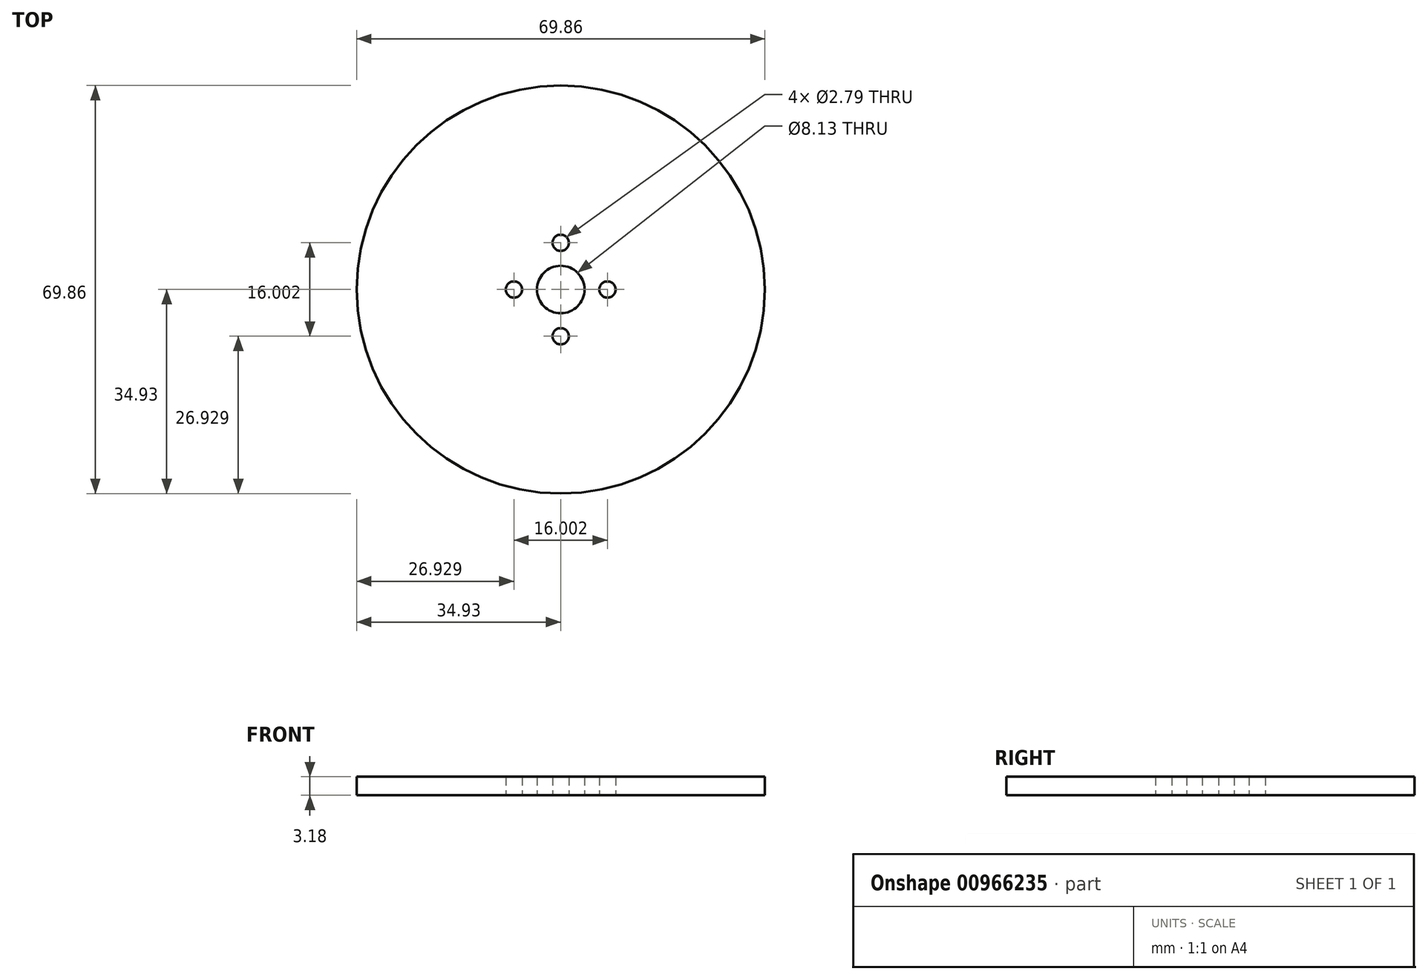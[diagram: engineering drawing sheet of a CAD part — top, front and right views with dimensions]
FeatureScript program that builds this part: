
annotation { "Feature Type Name" : "Feature", "Feature Type Description" : "" }
export const myFeature = defineFeature(function(context is Context, id is Id, definition is map)
    precondition{}
    {
        {
            var Q0;
            Q0=qCreatedBy(makeId("Top.planeOp"),FACE);
            var sketch = newSketch(context, id + "F0", { "sketchPlane" : qUnion([Q0])});
            skCircle(sketch, "E0", {"center": v(0, 0) * mm, "radius": 34.93 * mm});
            skCircle(sketch, "E1", {"center": v(0, 0) * mm, "radius": 4.06 * mm});
            skCircle(sketch, "E2", {"center": v(0, 8) * mm, "radius": 1.4 * mm});
            skCircle(sketch, "E3.1.0", {"center": v(-8, 0) * mm, "radius": 1.4 * mm});
            skCircle(sketch, "E3.2.0", {"center": v(0, -8) * mm, "radius": 1.4 * mm});
            skCircle(sketch, "E3.3.0", {"center": v(8, 0) * mm, "radius": 1.4 * mm});
            skSolve(sketch);
        }
        {
            var Q0;
            Q0=makeQuery(id+"F0.imprint","IMPRINT",FACE,{"disambiguationData":[TD([[makeQuery(id+"F0.imprint","IMPRINT",EDGE,{"derivedFrom":sQuery(id+"F0.wireOp",EDGE,"E0")}),1.0]])]});
            extrude(context, id + "F1", {"entities" : qUnion([Q0]), "depth" : 3.17 * mm});
        }
    });
